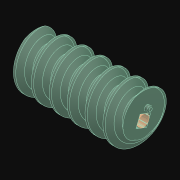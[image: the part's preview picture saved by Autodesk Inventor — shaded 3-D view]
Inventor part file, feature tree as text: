
AUTODESK INVENTOR PART (.ipt)
format: ipt  version: 2021.3 (Build 253353010, 353A)  size: 964,608 bytes
history: native  units: in
note: dims shown in document units (in); Inventor stores cm internally (conversion verified against a paired STEP export)
features: other x2, sketch x1, extrude x1
ambient origin geometry x8: Origin, YZ Plane, XZ Plane, XY Plane, X Axis, Y Axis, Z Axis, Center Point
bodies: Solid1 (feature_tree)
feature tree (4):
  sketch  "Sketch1"  dims[d0=0.3937in d1=0.0in]
  other  "Srf1"
  other  "Body-Move_Copy1"
  extrude  "ExtrusionSrf1"  [1 undecoded]
note: 1 required parameter value undecoded (feature->parameter linkage not recoverable at this tier; creation-order binding heuristic only, values carry confidence <= 0.55)
